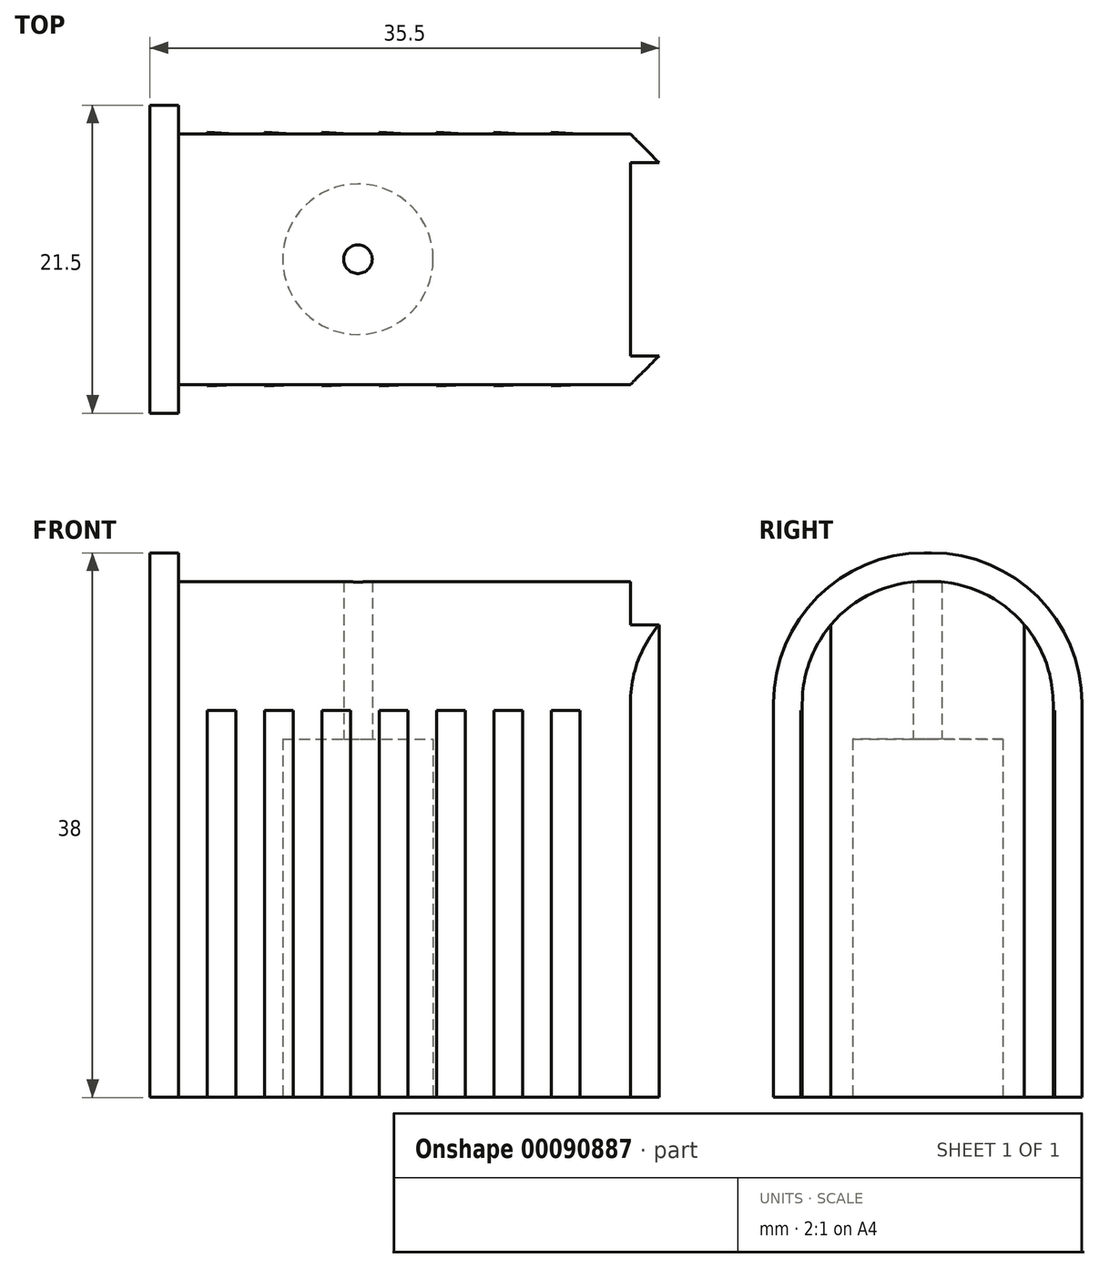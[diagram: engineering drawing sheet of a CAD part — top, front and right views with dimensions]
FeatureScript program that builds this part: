
annotation { "Feature Type Name" : "Feature", "Feature Type Description" : "" }
export const myFeature = defineFeature(function(context is Context, id is Id, definition is map)
    precondition{}
    {
        {
            var Q0;
            Q0=qCreatedBy(makeId("Right.planeOp"),FACE);
            var sketch = newSketch(context, id + "F0", { "sketchPlane" : qUnion([Q0])});
            skLineSegment(sketch, "E0.bottom", {"start": v(51.48, -63.8) * mm, "end": v(33.98, -63.8) * mm});
            skLineSegment(sketch, "E0.top", {"start": v(42.98, -27.8) * mm, "end": v(42.48, -27.8) * mm});
            skLineSegment(sketch, "E0.left", {"start": v(51.48, -63.8) * mm, "end": v(51.48, -36.3) * mm});
            skLineSegment(sketch, "E0.right", {"start": v(33.98, -63.8) * mm, "end": v(33.98, -36.3) * mm});
            skPoint(sketch, "E1.visualSharp", {"position": v(51.48, -27.8) * mm});
            skArc(sketch, "E1.filletArc", {"start": v(51.48, -36.3) * mm, "mid": v(48.99, -30.29) * mm, "end": v(42.98, -27.8) * mm});
            skPoint(sketch, "E2.visualSharp", {"position": v(33.98, -27.8) * mm});
            skArc(sketch, "E2.filletArc", {"start": v(42.48, -27.8) * mm, "mid": v(36.47, -30.29) * mm, "end": v(33.98, -36.3) * mm});
            skLineSegment(sketch, "E3.bottom", {"start": v(53.48, -63.8) * mm, "end": v(31.98, -63.8) * mm});
            skLineSegment(sketch, "E3.top", {"start": v(42.98, -25.8) * mm, "end": v(42.48, -25.8) * mm});
            skLineSegment(sketch, "E3.left", {"start": v(53.48, -63.8) * mm, "end": v(53.48, -36.3) * mm});
            skLineSegment(sketch, "E3.right", {"start": v(31.98, -63.8) * mm, "end": v(31.98, -36.3) * mm});
            skPoint(sketch, "E4.visualSharp", {"position": v(53.48, -25.8) * mm});
            skArc(sketch, "E4.filletArc", {"start": v(53.48, -36.3) * mm, "mid": v(50.4, -28.87) * mm, "end": v(42.98, -25.8) * mm});
            skPoint(sketch, "E5.visualSharp", {"position": v(31.98, -25.8) * mm});
            skArc(sketch, "E5.filletArc", {"start": v(42.48, -25.8) * mm, "mid": v(35.05, -28.87) * mm, "end": v(31.98, -36.3) * mm});
            skLineSegment(sketch, "E6", {"start": v(49.48, -63.8) * mm, "end": v(49.48, -30.82) * mm});
            skLineSegment(sketch, "E7", {"start": v(35.98, -63.8) * mm, "end": v(35.98, -30.82) * mm});
            skSolve(sketch);
        }
        {
            var Q0;
            Q0=makeQuery(id+"F0.imprint","IMPRINT",FACE,{"disambiguationData":[TD([[makeQuery(id+"F0.imprint","IMPRINT",EDGE,{"derivedFrom":sQuery(id+"F0.wireOp",EDGE,"E0.bottom")}),-1.0]])]});
            var Q1;
            {var subQ0=sQuery(id+"F0.wireOp",EDGE,"E0.left");Q1=makeQuery(id+"F0.imprint","IMPRINT",FACE,{"disambiguationData":[TD([[makeQuery(id+"F0.imprint","IMPRINT",EDGE,{"derivedFrom":subQ0}),1.0]])]});}
            var Q2;
            {var subQ0=sQuery(id+"F0.wireOp",EDGE,"E0.right");Q2=makeQuery(id+"F0.imprint","IMPRINT",FACE,{"disambiguationData":[TD([[makeQuery(id+"F0.imprint","IMPRINT",EDGE,{"derivedFrom":subQ0}),-1.0]])]});}
            extrude(context, id + "F1", {"entities" : qUnion([Q0, Q1, Q2]), "depth" : 35.5 * mm});
        }
        {
            var Q0;
            Q0=makeQuery(id+"F0.imprint","IMPRINT",FACE,{"disambiguationData":[TD([[makeQuery(id+"F0.imprint","IMPRINT",EDGE,{"derivedFrom":sQuery(id+"F0.wireOp",EDGE,"E0.top")}),-1.0]])]});
            var Q1;
            {var subQ4=sQuery(id+"F0.wireOp",EDGE,"E0.top");Q1=makeQuery(id+"F0.imprint","IMPRINT",FACE,{"disambiguationData":[TD([[makeQuery(id+"F0.imprint","IMPRINT",EDGE,{"derivedFrom":subQ4}),1.0]])]});}
            extrude(context, id + "F2", {"entities" : qUnion([Q0, Q1]), "operationType" : NewBodyOperationType.ADD, "depth" : 2 * mm});
        }
        {
            var Q0;
            {var subQ0=sQuery(id+"F0.wireOp",EDGE,"E6");Q0=makeQuery(id+"F0.imprint","IMPRINT",FACE,{"disambiguationData":[TD([[makeQuery(id+"F0.imprint","IMPRINT",EDGE,{"derivedFrom":subQ0}),1.0]])]});}
            extrude(context, id + "F3", {"entities" : qUnion([Q0]), "operationType" : NewBodyOperationType.ADD, "depth" : 33.5 * mm});
        }
        {
            var Q0;
            {var subQ0=sQuery(id+"F0.wireOp",EDGE,"E3.bottom");var subQ1=makeQuery(id+"F0.imprint","INTERSECT",VERTEX,{"derivedFrom":[sQuery(id+"F0.wireOp",EDGE,"E0.right"),subQ0]});var subQ2=makeQuery(id+"F0.imprint","INTERSECT",VERTEX,{"derivedFrom":[subQ0,sQuery(id+"F0.wireOp",EDGE,"E6")]});var subQ4=makeQuery(id+"F0.imprint","INTERSECT",VERTEX,{"derivedFrom":[sQuery(id+"F0.wireOp",EDGE,"E0.left"),subQ0]});Q0=makeQuery(id+"F3.boolean.opBoolean","MERGE",FACE,{"derivedFrom":[makeQuery(id+"F2.boolean.opBoolean","MERGE",FACE,{"derivedFrom":[makeQuery(id+"F1.opExtrude","SWEPT_FACE",FACE,{"disambiguationData":[OSD([subQ0]),TDD([makeQuery(id+"F0.imprint","IMPRINT",EDGE,{"disambiguationData":[TD([[subQ4,-1.0]])],"derivedFrom":subQ0})])]}),makeQuery(id+"F1.opExtrude","SWEPT_FACE",FACE,{"disambiguationData":[OSD([subQ0]),TDD([makeQuery(id+"F0.imprint","IMPRINT",EDGE,{"disambiguationData":[TD([[subQ1,1.0]])],"derivedFrom":subQ0})])]}),makeQuery(id+"F2.opExtrude","SWEPT_FACE",FACE,{"disambiguationData":[OSD([subQ0]),TDD([makeQuery(id+"F0.imprint","IMPRINT",EDGE,{"disambiguationData":[TD([[subQ4,1.0]])],"derivedFrom":subQ0})])]}),makeQuery(id+"F2.opExtrude","SWEPT_FACE",FACE,{"disambiguationData":[OSD([subQ0]),TDD([makeQuery(id+"F0.imprint","IMPRINT",EDGE,{"disambiguationData":[TD([[subQ2,-1.0]])],"derivedFrom":subQ0})])]}),makeQuery(id+"F2.opExtrude","SWEPT_FACE",FACE,{"disambiguationData":[OSD([subQ0]),TDD([makeQuery(id+"F0.imprint","IMPRINT",EDGE,{"disambiguationData":[TD([[subQ1,-1.0]])],"derivedFrom":subQ0})])]})]}),makeQuery(id+"F3.opExtrude","SWEPT_FACE",FACE,{"disambiguationData":[OSD([subQ0])]})]});}
            var sketch = newSketch(context, id + "F4", { "sketchPlane" : qUnion([Q0])});
            skCircle(sketch, "E8", {"center": v(14.5, -42.73) * mm, "radius": 5.25 * mm});
            skCircle(sketch, "E9", {"center": v(14.5, -42.73) * mm, "radius": 1 * mm});
            skLineSegment(sketch, "E10", {"start": v(33.5, -35.98) * mm, "end": v(33.5, -33.98) * mm});
            skLineSegment(sketch, "E11", {"start": v(33.5, -33.98) * mm, "end": v(35.5, -35.98) * mm});
            skLineSegment(sketch, "E12", {"start": v(35.5, -35.98) * mm, "end": v(33.5, -35.98) * mm});
            skLineSegment(sketch, "E13", {"start": v(33.5, -49.48) * mm, "end": v(33.5, -51.48) * mm});
            skLineSegment(sketch, "E14", {"start": v(33.5, -51.48) * mm, "end": v(35.5, -49.48) * mm});
            skLineSegment(sketch, "E15", {"start": v(35.5, -49.48) * mm, "end": v(33.5, -49.48) * mm});
            skLineSegment(sketch, "E16", {"start": v(4, -33.98) * mm, "end": v(4, -33.88) * mm});
            skLineSegment(sketch, "E17", {"start": v(4, -33.88) * mm, "end": v(6, -33.98) * mm});
            skLineSegment(sketch, "E18", {"start": v(4, -51.48) * mm, "end": v(4, -51.58) * mm});
            skLineSegment(sketch, "E19", {"start": v(4, -51.58) * mm, "end": v(6, -51.48) * mm});
            skLineSegment(sketch, "E20.1.0.0", {"start": v(8, -51.48) * mm, "end": v(8, -51.58) * mm});
            skLineSegment(sketch, "E20.1.0.1", {"start": v(8, -51.58) * mm, "end": v(10, -51.48) * mm});
            skLineSegment(sketch, "E20.2.0.0", {"start": v(12, -51.48) * mm, "end": v(12, -51.58) * mm});
            skLineSegment(sketch, "E20.2.0.1", {"start": v(12, -51.58) * mm, "end": v(14, -51.48) * mm});
            skLineSegment(sketch, "E20.3.0.0", {"start": v(16, -51.48) * mm, "end": v(16, -51.58) * mm});
            skLineSegment(sketch, "E20.3.0.1", {"start": v(16, -51.58) * mm, "end": v(18, -51.48) * mm});
            skLineSegment(sketch, "E20.4.0.0", {"start": v(20, -51.48) * mm, "end": v(20, -51.58) * mm});
            skLineSegment(sketch, "E20.4.0.1", {"start": v(20, -51.58) * mm, "end": v(22, -51.48) * mm});
            skLineSegment(sketch, "E20.5.0.0", {"start": v(24, -51.48) * mm, "end": v(24, -51.58) * mm});
            skLineSegment(sketch, "E20.5.0.1", {"start": v(24, -51.58) * mm, "end": v(26, -51.48) * mm});
            skLineSegment(sketch, "E20.6.0.0", {"start": v(28, -51.48) * mm, "end": v(28, -51.58) * mm});
            skLineSegment(sketch, "E20.6.0.1", {"start": v(28, -51.58) * mm, "end": v(30, -51.48) * mm});
            skLineSegment(sketch, "E20.direction1", {"start": v(4, -51.58) * mm, "end": v(8, -51.58) * mm, "construction": true});
            skLineSegment(sketch, "E21.1.0.0", {"start": v(8, -33.88) * mm, "end": v(10, -33.98) * mm});
            skLineSegment(sketch, "E21.1.0.1", {"start": v(8, -33.98) * mm, "end": v(8, -33.88) * mm});
            skLineSegment(sketch, "E21.2.0.0", {"start": v(12, -33.88) * mm, "end": v(14, -33.98) * mm});
            skLineSegment(sketch, "E21.2.0.1", {"start": v(12, -33.98) * mm, "end": v(12, -33.88) * mm});
            skLineSegment(sketch, "E21.3.0.0", {"start": v(16, -33.88) * mm, "end": v(18, -33.98) * mm});
            skLineSegment(sketch, "E21.3.0.1", {"start": v(16, -33.98) * mm, "end": v(16, -33.88) * mm});
            skLineSegment(sketch, "E21.4.0.0", {"start": v(20, -33.88) * mm, "end": v(22, -33.98) * mm});
            skLineSegment(sketch, "E21.4.0.1", {"start": v(20, -33.98) * mm, "end": v(20, -33.88) * mm});
            skLineSegment(sketch, "E21.5.0.0", {"start": v(24, -33.88) * mm, "end": v(26, -33.98) * mm});
            skLineSegment(sketch, "E21.5.0.1", {"start": v(24, -33.98) * mm, "end": v(24, -33.88) * mm});
            skLineSegment(sketch, "E21.6.0.0", {"start": v(28, -33.88) * mm, "end": v(30, -33.98) * mm});
            skLineSegment(sketch, "E21.6.0.1", {"start": v(28, -33.98) * mm, "end": v(28, -33.88) * mm});
            skLineSegment(sketch, "E21.direction1", {"start": v(4, -33.88) * mm, "end": v(8, -33.88) * mm, "construction": true});
            skSolve(sketch);
        }
        {
            var Q0;
            Q0=makeQuery(id+"F4.imprint","IMPRINT",FACE,{"disambiguationData":[TD([[makeQuery(id+"F4.imprint","IMPRINT",EDGE,{"derivedFrom":sQuery(id+"F4.wireOp",EDGE,"E8")}),1.0]])]});
            extrude(context, id + "F5", {"entities" : qUnion([Q0]), "operationType" : NewBodyOperationType.REMOVE, "oppositeDirection" : true, "depth" : 25 * mm});
        }
        {
            var Q0;
            {var subQ0=sQuery(id+"F0.wireOp",EDGE,"E3.bottom");var subQ1=makeQuery(id+"F0.imprint","INTERSECT",VERTEX,{"derivedFrom":[sQuery(id+"F0.wireOp",EDGE,"E0.right"),subQ0]});var subQ2=makeQuery(id+"F0.imprint","INTERSECT",VERTEX,{"derivedFrom":[subQ0,sQuery(id+"F0.wireOp",EDGE,"E6")]});var subQ4=makeQuery(id+"F0.imprint","INTERSECT",VERTEX,{"derivedFrom":[sQuery(id+"F0.wireOp",EDGE,"E0.left"),subQ0]});Q0=makeQuery(id+"F5.boolean.opBoolean","SPLIT",FACE,{"disambiguationData":[TD([makeQuery(id+"F5.opExtrude","SWEPT_FACE",FACE,{"disambiguationData":[OSD([sQuery(id+"F4.wireOp",EDGE,"E9")])]})])],"derivedFrom":makeQuery(id+"F3.boolean.opBoolean","MERGE",FACE,{"derivedFrom":[makeQuery(id+"F2.boolean.opBoolean","MERGE",FACE,{"derivedFrom":[makeQuery(id+"F1.opExtrude","SWEPT_FACE",FACE,{"disambiguationData":[OSD([subQ0]),TDD([makeQuery(id+"F0.imprint","IMPRINT",EDGE,{"disambiguationData":[TD([[subQ4,-1.0]])],"derivedFrom":subQ0})])]}),makeQuery(id+"F1.opExtrude","SWEPT_FACE",FACE,{"disambiguationData":[OSD([subQ0]),TDD([makeQuery(id+"F0.imprint","IMPRINT",EDGE,{"disambiguationData":[TD([[subQ1,1.0]])],"derivedFrom":subQ0})])]}),makeQuery(id+"F2.opExtrude","SWEPT_FACE",FACE,{"disambiguationData":[OSD([subQ0]),TDD([makeQuery(id+"F0.imprint","IMPRINT",EDGE,{"disambiguationData":[TD([[subQ4,1.0]])],"derivedFrom":subQ0})])]}),makeQuery(id+"F2.opExtrude","SWEPT_FACE",FACE,{"disambiguationData":[OSD([subQ0]),TDD([makeQuery(id+"F0.imprint","IMPRINT",EDGE,{"disambiguationData":[TD([[subQ2,-1.0]])],"derivedFrom":subQ0})])]}),makeQuery(id+"F2.opExtrude","SWEPT_FACE",FACE,{"disambiguationData":[OSD([subQ0]),TDD([makeQuery(id+"F0.imprint","IMPRINT",EDGE,{"disambiguationData":[TD([[subQ1,-1.0]])],"derivedFrom":subQ0})])]})]}),makeQuery(id+"F3.opExtrude","SWEPT_FACE",FACE,{"disambiguationData":[OSD([subQ0])]})]})});}
            extrude(context, id + "F6", {"entities" : qUnion([Q0]), "operationType" : NewBodyOperationType.REMOVE, "endBound" : BoundingType.UP_TO_NEXT, "oppositeDirection" : true, "depth" : 25 * mm});
        }
        {
            var Q0;
            {var subQ0=sQuery(id+"F4.wireOp",EDGE,"E14");Q0=makeQuery(id+"F4.imprint","IMPRINT",FACE,{"disambiguationData":[TD([[makeQuery(id+"F4.imprint","IMPRINT",EDGE,{"derivedFrom":subQ0}),-1.0]])]});}
            var Q1;
            {var subQ0=sQuery(id+"F4.wireOp",EDGE,"E11");Q1=makeQuery(id+"F4.imprint","IMPRINT",FACE,{"disambiguationData":[TD([[makeQuery(id+"F4.imprint","IMPRINT",EDGE,{"derivedFrom":subQ0}),1.0]])]});}
            extrude(context, id + "F7", {"entities" : qUnion([Q0, Q1]), "operationType" : NewBodyOperationType.REMOVE, "endBound" : BoundingType.UP_TO_NEXT, "oppositeDirection" : true, "depth" : 25 * mm});
        }
        {
            var Q0;
            {var subQ0=sQuery(id+"F4.wireOp",EDGE,"E18");Q0=makeQuery(id+"F4.imprint","IMPRINT",FACE,{"disambiguationData":[TD([[makeQuery(id+"F4.imprint","IMPRINT",EDGE,{"derivedFrom":subQ0}),1.0]])]});}
            var Q1;
            {var subQ0=sQuery(id+"F4.wireOp",EDGE,"E20.1.0.0");Q1=makeQuery(id+"F4.imprint","IMPRINT",FACE,{"disambiguationData":[TD([[makeQuery(id+"F4.imprint","IMPRINT",EDGE,{"derivedFrom":subQ0}),1.0]])]});}
            var Q2;
            {var subQ0=sQuery(id+"F4.wireOp",EDGE,"E20.6.0.0");Q2=makeQuery(id+"F4.imprint","IMPRINT",FACE,{"disambiguationData":[TD([[makeQuery(id+"F4.imprint","IMPRINT",EDGE,{"derivedFrom":subQ0}),1.0]])]});}
            var Q3;
            {var subQ0=sQuery(id+"F4.wireOp",EDGE,"E20.5.0.0");Q3=makeQuery(id+"F4.imprint","IMPRINT",FACE,{"disambiguationData":[TD([[makeQuery(id+"F4.imprint","IMPRINT",EDGE,{"derivedFrom":subQ0}),1.0]])]});}
            var Q4;
            {var subQ0=sQuery(id+"F4.wireOp",EDGE,"E20.4.0.0");Q4=makeQuery(id+"F4.imprint","IMPRINT",FACE,{"disambiguationData":[TD([[makeQuery(id+"F4.imprint","IMPRINT",EDGE,{"derivedFrom":subQ0}),1.0]])]});}
            var Q5;
            {var subQ0=sQuery(id+"F4.wireOp",EDGE,"E20.3.0.0");Q5=makeQuery(id+"F4.imprint","IMPRINT",FACE,{"disambiguationData":[TD([[makeQuery(id+"F4.imprint","IMPRINT",EDGE,{"derivedFrom":subQ0}),1.0]])]});}
            var Q6;
            {var subQ0=sQuery(id+"F4.wireOp",EDGE,"E20.2.0.0");Q6=makeQuery(id+"F4.imprint","IMPRINT",FACE,{"disambiguationData":[TD([[makeQuery(id+"F4.imprint","IMPRINT",EDGE,{"derivedFrom":subQ0}),1.0]])]});}
            var Q7;
            {var subQ0=sQuery(id+"F4.wireOp",EDGE,"E21.6.0.0");Q7=makeQuery(id+"F4.imprint","IMPRINT",FACE,{"disambiguationData":[TD([[makeQuery(id+"F4.imprint","IMPRINT",EDGE,{"derivedFrom":subQ0}),-1.0]])]});}
            var Q8;
            {var subQ0=sQuery(id+"F4.wireOp",EDGE,"E21.5.0.0");Q8=makeQuery(id+"F4.imprint","IMPRINT",FACE,{"disambiguationData":[TD([[makeQuery(id+"F4.imprint","IMPRINT",EDGE,{"derivedFrom":subQ0}),-1.0]])]});}
            var Q9;
            {var subQ0=sQuery(id+"F4.wireOp",EDGE,"E21.4.0.0");Q9=makeQuery(id+"F4.imprint","IMPRINT",FACE,{"disambiguationData":[TD([[makeQuery(id+"F4.imprint","IMPRINT",EDGE,{"derivedFrom":subQ0}),-1.0]])]});}
            var Q10;
            {var subQ0=sQuery(id+"F4.wireOp",EDGE,"E21.3.0.0");Q10=makeQuery(id+"F4.imprint","IMPRINT",FACE,{"disambiguationData":[TD([[makeQuery(id+"F4.imprint","IMPRINT",EDGE,{"derivedFrom":subQ0}),-1.0]])]});}
            var Q11;
            {var subQ0=sQuery(id+"F4.wireOp",EDGE,"E21.2.0.0");Q11=makeQuery(id+"F4.imprint","IMPRINT",FACE,{"disambiguationData":[TD([[makeQuery(id+"F4.imprint","IMPRINT",EDGE,{"derivedFrom":subQ0}),-1.0]])]});}
            var Q12;
            {var subQ0=sQuery(id+"F4.wireOp",EDGE,"E21.1.0.0");Q12=makeQuery(id+"F4.imprint","IMPRINT",FACE,{"disambiguationData":[TD([[makeQuery(id+"F4.imprint","IMPRINT",EDGE,{"derivedFrom":subQ0}),-1.0]])]});}
            var Q13;
            {var subQ0=sQuery(id+"F4.wireOp",EDGE,"E16");Q13=makeQuery(id+"F4.imprint","IMPRINT",FACE,{"disambiguationData":[TD([[makeQuery(id+"F4.imprint","IMPRINT",EDGE,{"derivedFrom":subQ0}),-1.0]])]});}
            extrude(context, id + "F8", {"entities" : qUnion([Q0, Q1, Q2, Q3, Q4, Q5, Q6, Q7, Q8, Q9, Q10, Q11, Q12, Q13]), "operationType" : NewBodyOperationType.ADD, "oppositeDirection" : true, "depth" : 27 * mm});
        }
    });
